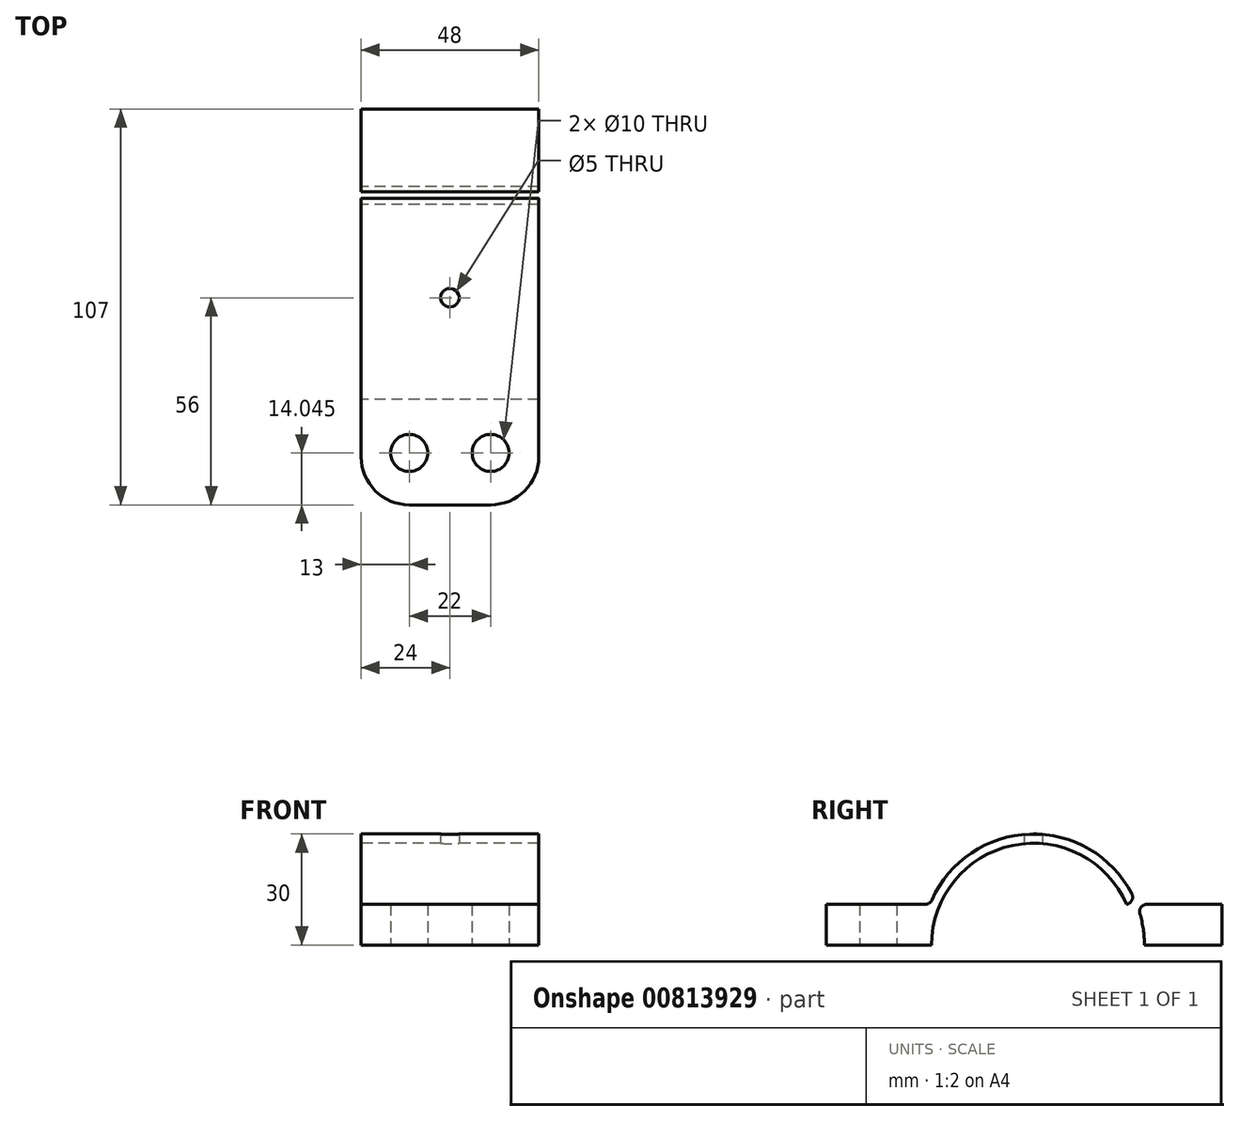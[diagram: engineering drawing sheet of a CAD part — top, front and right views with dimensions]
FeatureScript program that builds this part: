
annotation { "Feature Type Name" : "Feature", "Feature Type Description" : "" }
export const myFeature = defineFeature(function(context is Context, id is Id, definition is map)
    precondition{}
    {
        {
            var Q0;
            Q0=qCreatedBy(makeId("Right.planeOp"),FACE);
            var sketch = newSketch(context, id + "F0", { "sketchPlane" : qUnion([Q0])});
            skCircle(sketch, "E0", {"center": v(0, 0) * mm, "radius": 27.5 * mm});
            skCircle(sketch, "E1", {"center": v(0, 0) * mm, "radius": 30 * mm});
            skLineSegment(sketch, "E2.bottom", {"start": v(-56, 0) * mm, "end": v(51, 0) * mm});
            skLineSegment(sketch, "E2.top", {"start": v(-56, 11) * mm, "end": v(51, 11) * mm});
            skLineSegment(sketch, "E2.left", {"start": v(-56, 0) * mm, "end": v(-56, 11) * mm});
            skLineSegment(sketch, "E2.right", {"start": v(51, 0) * mm, "end": v(51, 11) * mm});
            skLineSegment(sketch, "E3.bottom", {"start": v(51, 11) * mm, "end": v(40, 11) * mm});
            skSolve(sketch);
        }
        {
            var Q0;
            {var subQ0=sQuery(id+"F0.wireOp",EDGE,"E2.left");Q0=makeQuery(id+"F0.imprint","IMPRINT",FACE,{"disambiguationData":[TD([[makeQuery(id+"F0.imprint","IMPRINT",EDGE,{"derivedFrom":subQ0}),-1.0]])]});}
            var Q1;
            {var subQ0=sQuery(id+"F0.wireOp",EDGE,"E2.top");var subQ1=sQuery(id+"F0.wireOp",EDGE,"E0");var subQ2=makeQuery(id+"F0.imprint","INTERSECT",VERTEX,{"disambiguationData":[OD(1.0)],"derivedFrom":[subQ1,subQ0]});Q1=makeQuery(id+"F0.imprint","IMPRINT",FACE,{"disambiguationData":[TD([[makeQuery(id+"F0.imprint","IMPRINT",EDGE,{"disambiguationData":[TD([[subQ2,-1.0]])],"derivedFrom":subQ1}),-1.0]])]});}
            var Q2;
            {var subQ0=sQuery(id+"F0.wireOp",EDGE,"E2.top");var subQ1=sQuery(id+"F0.wireOp",EDGE,"E0");var subQ2=makeQuery(id+"F0.imprint","INTERSECT",VERTEX,{"disambiguationData":[OD(0.0)],"derivedFrom":[subQ1,subQ0]});Q2=makeQuery(id+"F0.imprint","IMPRINT",FACE,{"disambiguationData":[TD([[makeQuery(id+"F0.imprint","IMPRINT",EDGE,{"disambiguationData":[TD([[subQ2,-1.0]])],"derivedFrom":subQ1}),-1.0]])]});}
            var Q3;
            {var subQ0=sQuery(id+"F0.wireOp",EDGE,"E2.top");var subQ1=sQuery(id+"F0.wireOp",EDGE,"E0");var subQ2=makeQuery(id+"F0.imprint","INTERSECT",VERTEX,{"disambiguationData":[OD(0.0)],"derivedFrom":[subQ1,subQ0]});Q3=makeQuery(id+"F0.imprint","IMPRINT",FACE,{"disambiguationData":[TD([[makeQuery(id+"F0.imprint","IMPRINT",EDGE,{"disambiguationData":[TD([[subQ2,1.0]])],"derivedFrom":subQ1}),-1.0]])]});}
            var Q4;
            {var subQ4=sQuery(id+"F0.wireOp",EDGE,"E2.right");Q4=makeQuery(id+"F0.imprint","IMPRINT",FACE,{"disambiguationData":[TD([[makeQuery(id+"F0.imprint","IMPRINT",EDGE,{"derivedFrom":subQ4}),1.0]])]});}
            var Q5;
            Q5=makeQuery(id+"F0.imprint","IMPRINT",FACE,{"disambiguationData":[TD([[makeQuery(id+"F0.imprint","IMPRINT",EDGE,{"derivedFrom":sQuery(id+"F0.wireOp",EDGE,"E3.bottom")}),-1.0]])]});
            extrude(context, id + "F1", {"entities" : qUnion([Q0, Q1, Q2, Q3, Q4, Q5]), "endBound" : BoundingType.SYMMETRIC, "depth" : 48 * mm});
        }
        {
            var Q0;
            Q0=qCreatedBy(makeId("Top.planeOp"),FACE);
            var sketch = newSketch(context, id + "F2", { "sketchPlane" : qUnion([Q0])});
            skCircle(sketch, "E4", {"center": v(0, 0) * mm, "radius": 2.5 * mm});
            skLineSegment(sketch, "E5", {"start": v(24, -41.96) * mm, "end": v(-24, -41.96) * mm, "construction": true});
            skLineSegment(sketch, "E6", {"start": v(0, -56) * mm, "end": v(0, -27.91) * mm, "construction": true});
            skCircle(sketch, "E7", {"center": v(-11, -41.96) * mm, "radius": 5 * mm});
            skCircle(sketch, "E8", {"center": v(11, -41.96) * mm, "radius": 5 * mm});
            skSolve(sketch);
        }
        {
            var Q0;
            Q0=qSketchRegion(id+"F2",true);
            extrude(context, id + "F3", {"entities" : qUnion([Q0]), "operationType" : NewBodyOperationType.REMOVE, "endBound" : BoundingType.THROUGH_ALL, "depth" : 25 * mm, "offsetDistance" : 25 * mm});
        }
        {
            var Q0;
            Q0=makeQuery(id+"F1.opExtrude","CAP_EDGE",EDGE,{"disambiguationData":[OSD([sQuery(id+"F0.wireOp",EDGE,"E2.left")])],"isStart":false});
            var Q1;
            Q1=makeQuery(id+"F1.opExtrude","CAP_EDGE",EDGE,{"disambiguationData":[OSD([sQuery(id+"F0.wireOp",EDGE,"E2.left")])],"isStart":true});
            fillet(context, id + "F4", {"entities" : qUnion([Q0, Q1]), "radius" : 13 * mm, "tangentPropagation" : true, "allowEdgeOverflow" : false});
        }
        {
            var Q0;
            {var subQ0=sQuery(id+"F0.wireOp",EDGE,"E1");var subQ1=sQuery(id+"F0.wireOp",EDGE,"E2.top");Q0=makeQuery(id+"F1.opExtrude","SWEPT_EDGE",EDGE,{"disambiguationData":[OSD([subQ0,subQ1]),TDD([makeQuery(id+"F0.imprint","INTERSECT",VERTEX,{"disambiguationData":[OD(1.0)],"derivedFrom":[subQ0,subQ1]})])]});}
            var Q1;
            {var subQ0=sQuery(id+"F0.wireOp",EDGE,"E1");var subQ1=sQuery(id+"F0.wireOp",EDGE,"E2.top");Q1=makeQuery(id+"F1.opExtrude","SWEPT_EDGE",EDGE,{"disambiguationData":[OSD([subQ0,subQ1]),TDD([makeQuery(id+"F0.imprint","INTERSECT",VERTEX,{"disambiguationData":[OD(0.0)],"derivedFrom":[subQ0,subQ1]})])]});}
            fillet(context, id + "F5", {"entities" : qUnion([Q0, Q1]), "radius" : 2 * mm, "tangentPropagation" : true, "allowEdgeOverflow" : false});
        }
    });
